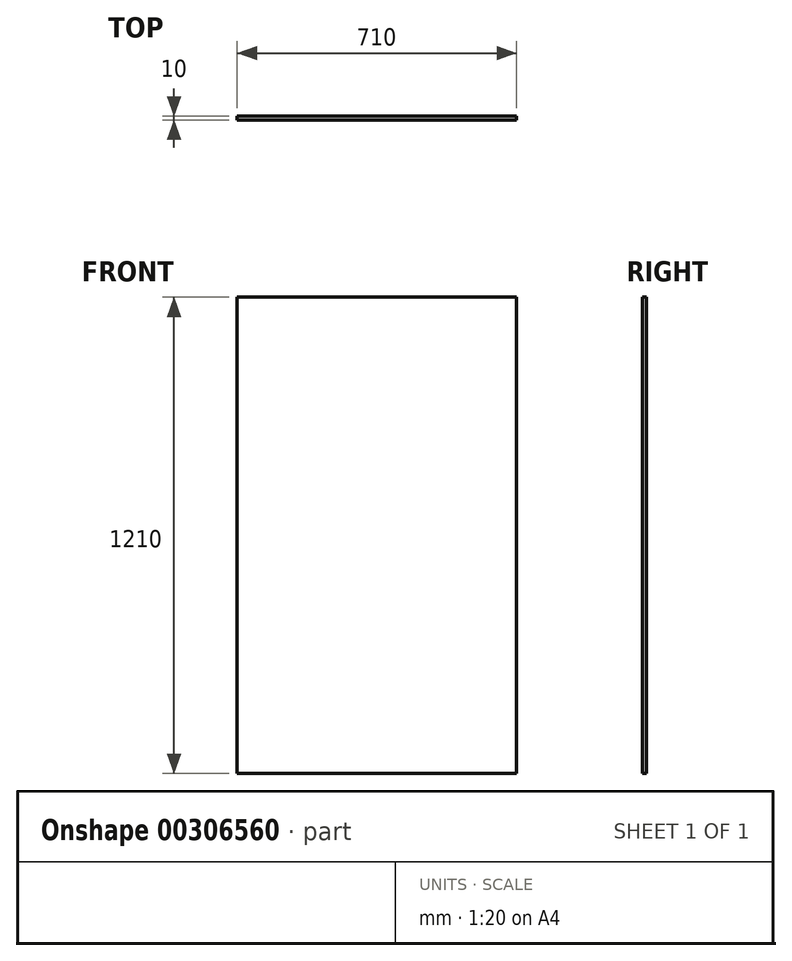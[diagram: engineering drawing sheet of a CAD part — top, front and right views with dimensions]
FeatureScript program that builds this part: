
annotation { "Feature Type Name" : "Feature", "Feature Type Description" : "" }
export const myFeature = defineFeature(function(context is Context, id is Id, definition is map)
    precondition{}
    {
        {
            var Q0;
            Q0=qCreatedBy(makeId("Front.planeOp"),FACE);
            var sketch = newSketch(context, id + "F0", { "sketchPlane" : qUnion([Q0])});
            skLineSegment(sketch, "E0.bottom", {"start": v(0, 0) * mm, "end": v(710, 0) * mm});
            skLineSegment(sketch, "E0.top", {"start": v(0, -1210) * mm, "end": v(710, -1210) * mm});
            skLineSegment(sketch, "E0.left", {"start": v(0, 0) * mm, "end": v(0, -1210) * mm});
            skLineSegment(sketch, "E0.right", {"start": v(710, 0) * mm, "end": v(710, -1210) * mm});
            skSolve(sketch);
        }
        {
            var Q0;
            Q0=makeQuery(id+"F0.imprint","IMPRINT",FACE,{"disambiguationData":[TD([[makeQuery(id+"F0.imprint","IMPRINT",EDGE,{"derivedFrom":sQuery(id+"F0.wireOp",EDGE,"E0.bottom")}),-1.0]])]});
            extrude(context, id + "F1", {"entities" : qUnion([Q0]), "depth" : 10 * mm});
        }
    });
